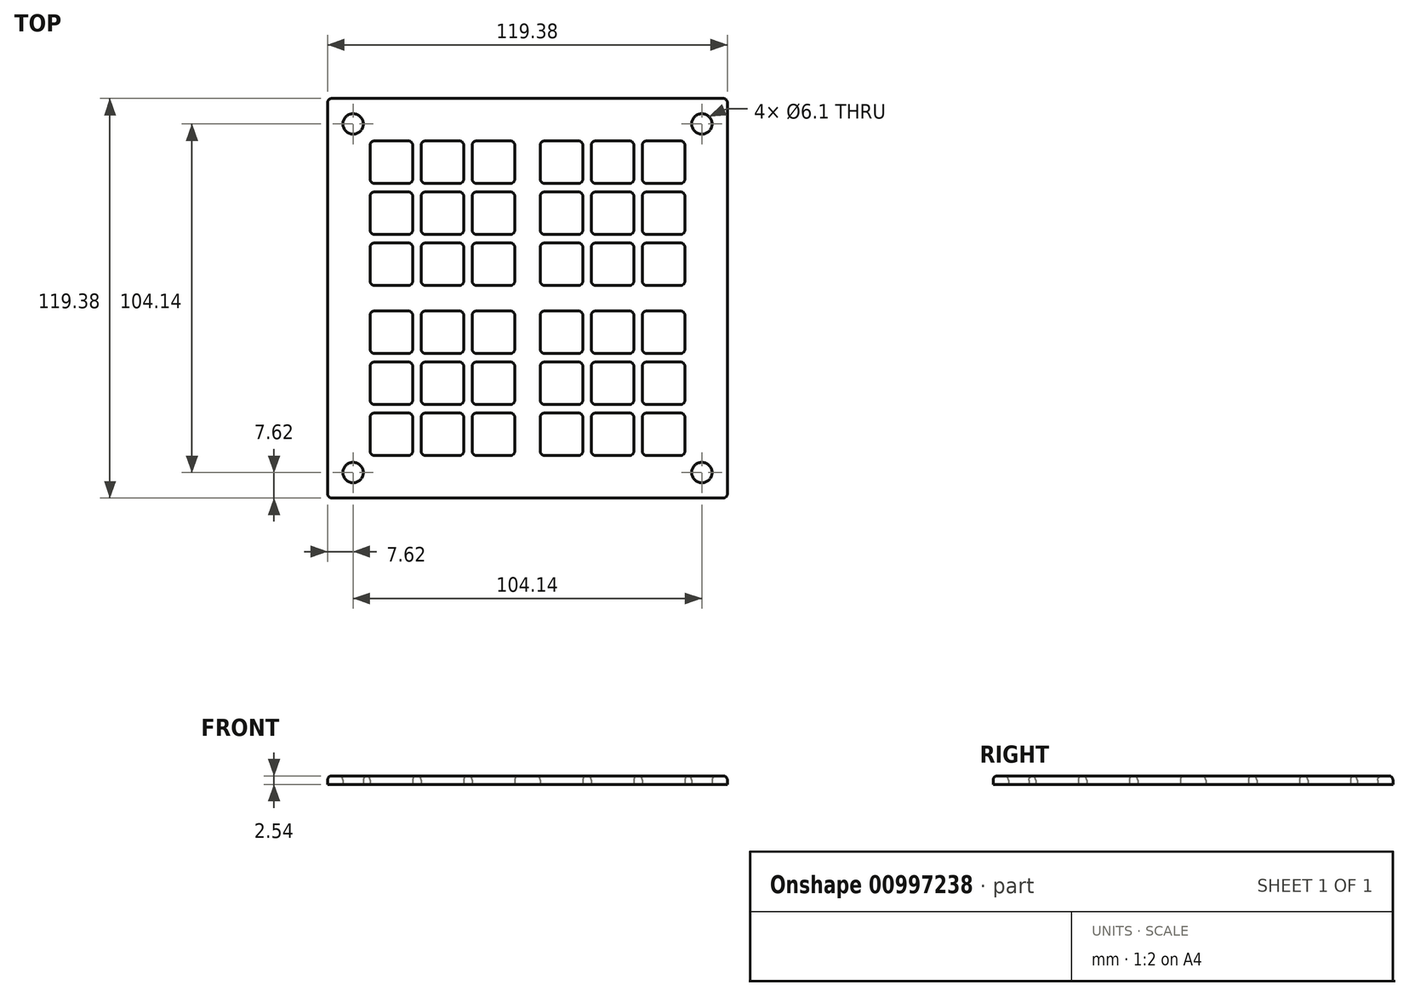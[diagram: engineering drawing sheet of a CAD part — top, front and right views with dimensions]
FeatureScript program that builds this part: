
annotation { "Feature Type Name" : "Feature", "Feature Type Description" : "" }
export const myFeature = defineFeature(function(context is Context, id is Id, definition is map)
    precondition{}
    {
        {
            var Q0;
            Q0=qCreatedBy(makeId("Top.planeOp"),FACE);
            var sketch = newSketch(context, id + "F0", { "sketchPlane" : qUnion([Q0])});
            skLineSegment(sketch, "E0.bottom", {"start": v(59.69, -59.7) * mm, "end": v(-59.7, -59.69) * mm});
            skLineSegment(sketch, "E0.top", {"start": v(59.7, 59.69) * mm, "end": v(-59.7, 59.7) * mm});
            skLineSegment(sketch, "E0.left", {"start": v(59.69, -59.7) * mm, "end": v(59.7, 59.69) * mm});
            skLineSegment(sketch, "E0.right", {"start": v(-59.7, -59.69) * mm, "end": v(-59.69, 59.69) * mm});
            skPoint(sketch, "E0.middle", {"position": v(0, 0) * mm});
            skCircle(sketch, "E1", {"center": v(52.07, -52.07) * mm, "radius": 3.05 * mm});
            skLineSegment(sketch, "E2", {"start": v(0, 59.7) * mm, "end": v(0, -59.7) * mm, "construction": true});
            skLineSegment(sketch, "E3", {"start": v(59.7, 0) * mm, "end": v(-59.7, 0) * mm, "construction": true});
            skCircle(sketch, "E4.MirrorC", {"center": v(-52.07, -52.07) * mm, "radius": 3.05 * mm});
            skCircle(sketch, "E5.MirrorC", {"center": v(52.07, 52.07) * mm, "radius": 3.05 * mm});
            skCircle(sketch, "E6.MirrorC", {"center": v(-52.07, 52.07) * mm, "radius": 3.05 * mm});
            skLineSegment(sketch, "E7.bottom", {"start": v(35.56, -34.3) * mm, "end": v(45.72, -34.3) * mm});
            skLineSegment(sketch, "E7.top", {"start": v(35.56, -47) * mm, "end": v(45.72, -47) * mm});
            skLineSegment(sketch, "E7.left", {"start": v(34.3, -35.56) * mm, "end": v(34.3, -45.72) * mm});
            skLineSegment(sketch, "E7.right", {"start": v(47, -35.56) * mm, "end": v(47, -45.72) * mm});
            skPoint(sketch, "E7.middle", {"position": v(40.64, -40.64) * mm});
            skPoint(sketch, "E8.visualSharp", {"position": v(46.99, -47) * mm});
            skArc(sketch, "E8.filletArc", {"start": v(45.72, -47) * mm, "mid": v(46.62, -46.62) * mm, "end": v(46.99, -45.72) * mm});
            skPoint(sketch, "E9.visualSharp", {"position": v(34.3, -47) * mm});
            skArc(sketch, "E9.filletArc", {"start": v(34.3, -45.72) * mm, "mid": v(34.66, -46.62) * mm, "end": v(35.56, -47) * mm});
            skPoint(sketch, "E10.visualSharp", {"position": v(34.3, -34.3) * mm});
            skArc(sketch, "E10.filletArc", {"start": v(35.56, -34.3) * mm, "mid": v(34.66, -34.66) * mm, "end": v(34.3, -35.56) * mm});
            skPoint(sketch, "E11.visualSharp", {"position": v(47, -34.3) * mm});
            skArc(sketch, "E11.filletArc", {"start": v(47, -35.56) * mm, "mid": v(46.62, -34.66) * mm, "end": v(45.72, -34.3) * mm});
            skLineSegment(sketch, "E12.0.1.0", {"start": v(34.3, -20.32) * mm, "end": v(34.3, -30.48) * mm});
            skLineSegment(sketch, "E12.0.1.1", {"start": v(35.56, -31.75) * mm, "end": v(45.72, -31.75) * mm});
            skLineSegment(sketch, "E12.0.1.2", {"start": v(47, -20.32) * mm, "end": v(47, -30.48) * mm});
            skLineSegment(sketch, "E12.0.1.3", {"start": v(35.56, -19.05) * mm, "end": v(45.72, -19.05) * mm});
            skArc(sketch, "E12.0.1.4", {"start": v(35.56, -19.05) * mm, "mid": v(34.66, -19.42) * mm, "end": v(34.3, -20.32) * mm});
            skArc(sketch, "E12.0.1.5", {"start": v(47, -20.32) * mm, "mid": v(46.62, -19.42) * mm, "end": v(45.72, -19.05) * mm});
            skArc(sketch, "E12.0.1.6", {"start": v(45.72, -31.75) * mm, "mid": v(46.62, -31.38) * mm, "end": v(46.99, -30.48) * mm});
            skArc(sketch, "E12.0.1.7", {"start": v(34.3, -30.48) * mm, "mid": v(34.66, -31.38) * mm, "end": v(35.56, -31.75) * mm});
            skLineSegment(sketch, "E12.0.2.0", {"start": v(34.3, -5.08) * mm, "end": v(34.3, -15.24) * mm});
            skLineSegment(sketch, "E12.0.2.1", {"start": v(35.56, -16.51) * mm, "end": v(45.72, -16.51) * mm});
            skLineSegment(sketch, "E12.0.2.2", {"start": v(47, -5.08) * mm, "end": v(47, -15.24) * mm});
            skLineSegment(sketch, "E12.0.2.3", {"start": v(35.56, -3.81) * mm, "end": v(45.72, -3.81) * mm});
            skArc(sketch, "E12.0.2.4", {"start": v(35.56, -3.81) * mm, "mid": v(34.66, -4.18) * mm, "end": v(34.3, -5.08) * mm});
            skArc(sketch, "E12.0.2.5", {"start": v(47, -5.08) * mm, "mid": v(46.62, -4.18) * mm, "end": v(45.72, -3.81) * mm});
            skArc(sketch, "E12.0.2.6", {"start": v(45.72, -16.51) * mm, "mid": v(46.62, -16.14) * mm, "end": v(46.99, -15.24) * mm});
            skArc(sketch, "E12.0.2.7", {"start": v(34.3, -15.24) * mm, "mid": v(34.66, -16.14) * mm, "end": v(35.56, -16.51) * mm});
            skLineSegment(sketch, "E12.1.0.0", {"start": v(19.05, -35.56) * mm, "end": v(19.05, -45.72) * mm});
            skLineSegment(sketch, "E12.1.0.1", {"start": v(20.32, -47) * mm, "end": v(30.48, -47) * mm});
            skLineSegment(sketch, "E12.1.0.2", {"start": v(31.75, -35.56) * mm, "end": v(31.75, -45.72) * mm});
            skLineSegment(sketch, "E12.1.0.3", {"start": v(20.32, -34.3) * mm, "end": v(30.48, -34.3) * mm});
            skArc(sketch, "E12.1.0.4", {"start": v(20.32, -34.3) * mm, "mid": v(19.42, -34.66) * mm, "end": v(19.05, -35.56) * mm});
            skArc(sketch, "E12.1.0.5", {"start": v(31.75, -35.56) * mm, "mid": v(31.38, -34.66) * mm, "end": v(30.48, -34.3) * mm});
            skArc(sketch, "E12.1.0.6", {"start": v(30.48, -47) * mm, "mid": v(31.38, -46.62) * mm, "end": v(31.75, -45.72) * mm});
            skArc(sketch, "E12.1.0.7", {"start": v(19.05, -45.72) * mm, "mid": v(19.42, -46.62) * mm, "end": v(20.32, -47) * mm});
            skLineSegment(sketch, "E12.1.1.0", {"start": v(19.05, -20.32) * mm, "end": v(19.05, -30.48) * mm});
            skLineSegment(sketch, "E12.1.1.1", {"start": v(20.32, -31.75) * mm, "end": v(30.48, -31.75) * mm});
            skLineSegment(sketch, "E12.1.1.2", {"start": v(31.75, -20.32) * mm, "end": v(31.75, -30.48) * mm});
            skLineSegment(sketch, "E12.1.1.3", {"start": v(20.32, -19.05) * mm, "end": v(30.48, -19.05) * mm});
            skArc(sketch, "E12.1.1.4", {"start": v(20.32, -19.05) * mm, "mid": v(19.42, -19.42) * mm, "end": v(19.05, -20.32) * mm});
            skArc(sketch, "E12.1.1.5", {"start": v(31.75, -20.32) * mm, "mid": v(31.38, -19.42) * mm, "end": v(30.48, -19.05) * mm});
            skArc(sketch, "E12.1.1.6", {"start": v(30.48, -31.75) * mm, "mid": v(31.38, -31.38) * mm, "end": v(31.75, -30.48) * mm});
            skArc(sketch, "E12.1.1.7", {"start": v(19.05, -30.48) * mm, "mid": v(19.42, -31.38) * mm, "end": v(20.32, -31.75) * mm});
            skLineSegment(sketch, "E12.1.2.0", {"start": v(19.05, -5.08) * mm, "end": v(19.05, -15.24) * mm});
            skLineSegment(sketch, "E12.1.2.1", {"start": v(20.32, -16.51) * mm, "end": v(30.48, -16.51) * mm});
            skLineSegment(sketch, "E12.1.2.2", {"start": v(31.75, -5.08) * mm, "end": v(31.75, -15.24) * mm});
            skLineSegment(sketch, "E12.1.2.3", {"start": v(20.32, -3.81) * mm, "end": v(30.48, -3.81) * mm});
            skArc(sketch, "E12.1.2.4", {"start": v(20.32, -3.81) * mm, "mid": v(19.42, -4.18) * mm, "end": v(19.05, -5.08) * mm});
            skArc(sketch, "E12.1.2.5", {"start": v(31.75, -5.08) * mm, "mid": v(31.38, -4.18) * mm, "end": v(30.48, -3.81) * mm});
            skArc(sketch, "E12.1.2.6", {"start": v(30.48, -16.51) * mm, "mid": v(31.38, -16.14) * mm, "end": v(31.75, -15.24) * mm});
            skArc(sketch, "E12.1.2.7", {"start": v(19.05, -15.24) * mm, "mid": v(19.42, -16.14) * mm, "end": v(20.32, -16.51) * mm});
            skLineSegment(sketch, "E12.2.0.0", {"start": v(3.81, -35.56) * mm, "end": v(3.81, -45.72) * mm});
            skLineSegment(sketch, "E12.2.0.1", {"start": v(5.08, -47) * mm, "end": v(15.24, -47) * mm});
            skLineSegment(sketch, "E12.2.0.2", {"start": v(16.51, -35.56) * mm, "end": v(16.51, -45.72) * mm});
            skLineSegment(sketch, "E12.2.0.3", {"start": v(5.08, -34.3) * mm, "end": v(15.24, -34.3) * mm});
            skArc(sketch, "E12.2.0.4", {"start": v(5.08, -34.3) * mm, "mid": v(4.18, -34.66) * mm, "end": v(3.81, -35.56) * mm});
            skArc(sketch, "E12.2.0.5", {"start": v(16.51, -35.56) * mm, "mid": v(16.14, -34.66) * mm, "end": v(15.24, -34.3) * mm});
            skArc(sketch, "E12.2.0.6", {"start": v(15.24, -47) * mm, "mid": v(16.14, -46.62) * mm, "end": v(16.51, -45.72) * mm});
            skArc(sketch, "E12.2.0.7", {"start": v(3.81, -45.72) * mm, "mid": v(4.18, -46.62) * mm, "end": v(5.08, -47) * mm});
            skLineSegment(sketch, "E12.2.1.0", {"start": v(3.81, -20.32) * mm, "end": v(3.81, -30.48) * mm});
            skLineSegment(sketch, "E12.2.1.1", {"start": v(5.08, -31.75) * mm, "end": v(15.24, -31.75) * mm});
            skLineSegment(sketch, "E12.2.1.2", {"start": v(16.51, -20.32) * mm, "end": v(16.51, -30.48) * mm});
            skLineSegment(sketch, "E12.2.1.3", {"start": v(5.08, -19.05) * mm, "end": v(15.24, -19.05) * mm});
            skArc(sketch, "E12.2.1.4", {"start": v(5.08, -19.05) * mm, "mid": v(4.18, -19.42) * mm, "end": v(3.81, -20.32) * mm});
            skArc(sketch, "E12.2.1.5", {"start": v(16.51, -20.32) * mm, "mid": v(16.14, -19.42) * mm, "end": v(15.24, -19.05) * mm});
            skArc(sketch, "E12.2.1.6", {"start": v(15.24, -31.75) * mm, "mid": v(16.14, -31.38) * mm, "end": v(16.51, -30.48) * mm});
            skArc(sketch, "E12.2.1.7", {"start": v(3.81, -30.48) * mm, "mid": v(4.18, -31.38) * mm, "end": v(5.08, -31.75) * mm});
            skLineSegment(sketch, "E12.2.2.0", {"start": v(3.81, -5.08) * mm, "end": v(3.81, -15.24) * mm});
            skLineSegment(sketch, "E12.2.2.1", {"start": v(5.08, -16.51) * mm, "end": v(15.24, -16.51) * mm});
            skLineSegment(sketch, "E12.2.2.2", {"start": v(16.51, -5.08) * mm, "end": v(16.51, -15.24) * mm});
            skLineSegment(sketch, "E12.2.2.3", {"start": v(5.08, -3.81) * mm, "end": v(15.24, -3.81) * mm});
            skArc(sketch, "E12.2.2.4", {"start": v(5.08, -3.81) * mm, "mid": v(4.18, -4.18) * mm, "end": v(3.81, -5.08) * mm});
            skArc(sketch, "E12.2.2.5", {"start": v(16.51, -5.08) * mm, "mid": v(16.14, -4.18) * mm, "end": v(15.24, -3.81) * mm});
            skArc(sketch, "E12.2.2.6", {"start": v(15.24, -16.51) * mm, "mid": v(16.14, -16.14) * mm, "end": v(16.51, -15.24) * mm});
            skArc(sketch, "E12.2.2.7", {"start": v(3.81, -15.24) * mm, "mid": v(4.18, -16.14) * mm, "end": v(5.08, -16.51) * mm});
            skLineSegment(sketch, "E12.direction1", {"start": v(36.51, -44.77) * mm, "end": v(21.27, -44.77) * mm, "construction": true});
            skLineSegment(sketch, "E12.direction2", {"start": v(36.51, -44.77) * mm, "end": v(36.51, -29.53) * mm, "construction": true});
            skArc(sketch, "E13.MirrorCS", {"start": v(-47, -35.56) * mm, "mid": v(-46.62, -34.66) * mm, "end": v(-45.72, -34.3) * mm});
            skArc(sketch, "E14.MirrorCS", {"start": v(-35.56, -34.3) * mm, "mid": v(-34.66, -34.66) * mm, "end": v(-34.29, -35.56) * mm});
            skArc(sketch, "E15.MirrorCS", {"start": v(-34.3, -45.72) * mm, "mid": v(-34.66, -46.62) * mm, "end": v(-35.56, -47) * mm});
            skArc(sketch, "E16.MirrorCS", {"start": v(-45.72, -47) * mm, "mid": v(-46.62, -46.62) * mm, "end": v(-46.99, -45.72) * mm});
            skArc(sketch, "E17.MirrorCS", {"start": v(-34.29, -30.48) * mm, "mid": v(-34.66, -31.38) * mm, "end": v(-35.56, -31.75) * mm});
            skArc(sketch, "E18.MirrorCS", {"start": v(-20.32, -19.05) * mm, "mid": v(-19.42, -19.42) * mm, "end": v(-19.05, -20.32) * mm});
            skArc(sketch, "E19.MirrorCS", {"start": v(-5.08, -34.3) * mm, "mid": v(-4.18, -34.66) * mm, "end": v(-3.8, -35.56) * mm});
            skArc(sketch, "E20.MirrorCS", {"start": v(-5.08, -3.81) * mm, "mid": v(-4.18, -4.18) * mm, "end": v(-3.81, -5.08) * mm});
            skArc(sketch, "E21.MirrorCS", {"start": v(-35.56, -3.81) * mm, "mid": v(-34.66, -4.18) * mm, "end": v(-34.3, -5.08) * mm});
            skArc(sketch, "E22.MirrorCS", {"start": v(-15.24, -47) * mm, "mid": v(-16.14, -46.62) * mm, "end": v(-16.5, -45.72) * mm});
            skArc(sketch, "E23.MirrorCS", {"start": v(-45.72, -16.51) * mm, "mid": v(-46.62, -16.14) * mm, "end": v(-46.99, -15.24) * mm});
            skArc(sketch, "E24.MirrorCS", {"start": v(-30.48, -47) * mm, "mid": v(-31.38, -46.62) * mm, "end": v(-31.75, -45.72) * mm});
            skArc(sketch, "E25.MirrorCS", {"start": v(-16.51, -5.08) * mm, "mid": v(-16.14, -4.18) * mm, "end": v(-15.24, -3.81) * mm});
            skArc(sketch, "E26.MirrorCS", {"start": v(-19.05, -30.48) * mm, "mid": v(-19.42, -31.38) * mm, "end": v(-20.32, -31.75) * mm});
            skArc(sketch, "E27.MirrorCS", {"start": v(-3.81, -15.24) * mm, "mid": v(-4.18, -16.14) * mm, "end": v(-5.08, -16.51) * mm});
            skArc(sketch, "E28.MirrorCS", {"start": v(-16.51, -35.56) * mm, "mid": v(-16.14, -34.66) * mm, "end": v(-15.24, -34.3) * mm});
            skArc(sketch, "E29.MirrorCS", {"start": v(-31.75, -20.32) * mm, "mid": v(-31.38, -19.42) * mm, "end": v(-30.48, -19.05) * mm});
            skArc(sketch, "E30.MirrorCS", {"start": v(-15.24, -31.75) * mm, "mid": v(-16.14, -31.38) * mm, "end": v(-16.5, -30.48) * mm});
            skArc(sketch, "E31.MirrorCS", {"start": v(-16.51, -20.32) * mm, "mid": v(-16.14, -19.42) * mm, "end": v(-15.24, -19.05) * mm});
            skArc(sketch, "E32.MirrorCS", {"start": v(-47, -20.32) * mm, "mid": v(-46.62, -19.42) * mm, "end": v(-45.72, -19.05) * mm});
            skArc(sketch, "E33.MirrorCS", {"start": v(-31.75, -35.56) * mm, "mid": v(-31.38, -34.66) * mm, "end": v(-30.48, -34.3) * mm});
            skArc(sketch, "E34.MirrorCS", {"start": v(-31.75, -5.08) * mm, "mid": v(-31.38, -4.18) * mm, "end": v(-30.48, -3.81) * mm});
            skArc(sketch, "E35.MirrorCS", {"start": v(-3.81, -30.48) * mm, "mid": v(-4.18, -31.38) * mm, "end": v(-5.08, -31.75) * mm});
            skArc(sketch, "E36.MirrorCS", {"start": v(-19.05, -45.72) * mm, "mid": v(-19.42, -46.62) * mm, "end": v(-20.32, -47) * mm});
            skArc(sketch, "E37.MirrorCS", {"start": v(-19.05, -15.24) * mm, "mid": v(-19.42, -16.14) * mm, "end": v(-20.32, -16.51) * mm});
            skArc(sketch, "E38.MirrorCS", {"start": v(-30.48, -31.75) * mm, "mid": v(-31.38, -31.38) * mm, "end": v(-31.75, -30.48) * mm});
            skArc(sketch, "E39.MirrorCS", {"start": v(-15.24, -16.51) * mm, "mid": v(-16.14, -16.14) * mm, "end": v(-16.51, -15.24) * mm});
            skArc(sketch, "E40.MirrorCS", {"start": v(-5.08, -19.05) * mm, "mid": v(-4.18, -19.42) * mm, "end": v(-3.81, -20.32) * mm});
            skArc(sketch, "E41.MirrorCS", {"start": v(-35.56, -19.05) * mm, "mid": v(-34.66, -19.42) * mm, "end": v(-34.3, -20.32) * mm});
            skArc(sketch, "E42.MirrorCS", {"start": v(-20.32, -34.3) * mm, "mid": v(-19.42, -34.66) * mm, "end": v(-19.05, -35.56) * mm});
            skArc(sketch, "E43.MirrorCS", {"start": v(-20.32, -3.81) * mm, "mid": v(-19.42, -4.18) * mm, "end": v(-19.05, -5.08) * mm});
            skArc(sketch, "E44.MirrorCS", {"start": v(-30.48, -16.51) * mm, "mid": v(-31.38, -16.14) * mm, "end": v(-31.75, -15.24) * mm});
            skArc(sketch, "E45.MirrorCS", {"start": v(-45.72, -31.75) * mm, "mid": v(-46.62, -31.38) * mm, "end": v(-46.99, -30.48) * mm});
            skArc(sketch, "E46.MirrorCS", {"start": v(-34.3, -15.24) * mm, "mid": v(-34.66, -16.14) * mm, "end": v(-35.56, -16.51) * mm});
            skArc(sketch, "E47.MirrorCS", {"start": v(-3.8, -45.72) * mm, "mid": v(-4.18, -46.62) * mm, "end": v(-5.08, -47) * mm});
            skArc(sketch, "E48.MirrorCS", {"start": v(-47, -5.08) * mm, "mid": v(-46.62, -4.18) * mm, "end": v(-45.72, -3.81) * mm});
            skLineSegment(sketch, "E49.MirrorCS", {"start": v(-5.08, -19.05) * mm, "end": v(-15.24, -19.05) * mm});
            skLineSegment(sketch, "E50.MirrorCS", {"start": v(-35.56, -19.05) * mm, "end": v(-45.72, -19.05) * mm});
            skLineSegment(sketch, "E51.MirrorCS", {"start": v(-20.32, -34.3) * mm, "end": v(-30.48, -34.3) * mm});
            skLineSegment(sketch, "E52.MirrorCS", {"start": v(-20.32, -3.81) * mm, "end": v(-30.48, -3.81) * mm});
            skLineSegment(sketch, "E53.MirrorCS", {"start": v(-46.99, -35.56) * mm, "end": v(-46.99, -45.72) * mm});
            skLineSegment(sketch, "E54.MirrorCS", {"start": v(-5.08, -31.75) * mm, "end": v(-15.24, -31.75) * mm});
            skLineSegment(sketch, "E55.MirrorCS", {"start": v(-36.51, -44.77) * mm, "end": v(-36.51, -29.53) * mm, "construction": true});
            skLineSegment(sketch, "E56.MirrorCS", {"start": v(-34.29, -35.56) * mm, "end": v(-34.29, -45.72) * mm});
            skLineSegment(sketch, "E57.MirrorCS", {"start": v(-20.32, -47) * mm, "end": v(-30.48, -47) * mm});
            skLineSegment(sketch, "E58.MirrorCS", {"start": v(-20.32, -16.51) * mm, "end": v(-30.48, -16.51) * mm});
            skLineSegment(sketch, "E59.MirrorCS", {"start": v(-3.81, -20.32) * mm, "end": v(-3.8, -30.48) * mm});
            skLineSegment(sketch, "E60.MirrorCS", {"start": v(-35.56, -47) * mm, "end": v(-45.72, -47) * mm});
            skLineSegment(sketch, "E61.MirrorCS", {"start": v(-36.51, -44.77) * mm, "end": v(-21.27, -44.77) * mm, "construction": true});
            skPoint(sketch, "E62.MirrorP", {"position": v(-34.29, -34.3) * mm});
            skLineSegment(sketch, "E63.MirrorCS", {"start": v(-35.56, -34.3) * mm, "end": v(-45.72, -34.3) * mm});
            skLineSegment(sketch, "E64.MirrorCS", {"start": v(-19.05, -35.56) * mm, "end": v(-19.05, -45.72) * mm});
            skLineSegment(sketch, "E65.MirrorCS", {"start": v(-19.05, -5.08) * mm, "end": v(-19.05, -15.24) * mm});
            skLineSegment(sketch, "E66.MirrorCS", {"start": v(-19.05, -20.32) * mm, "end": v(-19.05, -30.48) * mm});
            skLineSegment(sketch, "E67.MirrorCS", {"start": v(-3.81, -35.56) * mm, "end": v(-3.8, -45.72) * mm});
            skLineSegment(sketch, "E68.MirrorCS", {"start": v(-3.81, -5.08) * mm, "end": v(-3.81, -15.24) * mm});
            skLineSegment(sketch, "E69.MirrorCS", {"start": v(-34.3, -5.08) * mm, "end": v(-34.3, -15.24) * mm});
            skLineSegment(sketch, "E70.MirrorCS", {"start": v(-31.75, -20.32) * mm, "end": v(-31.75, -30.48) * mm});
            skLineSegment(sketch, "E71.MirrorCS", {"start": v(-16.51, -35.56) * mm, "end": v(-16.51, -45.72) * mm});
            skLineSegment(sketch, "E72.MirrorCS", {"start": v(-16.51, -5.08) * mm, "end": v(-16.51, -15.24) * mm});
            skLineSegment(sketch, "E73.MirrorCS", {"start": v(-47, -5.08) * mm, "end": v(-47, -15.24) * mm});
            skPoint(sketch, "E74.MirrorP", {"position": v(-46.99, -47) * mm});
            skPoint(sketch, "E75.MirrorP", {"position": v(-34.29, -47) * mm});
            skLineSegment(sketch, "E76.MirrorCS", {"start": v(-34.3, -20.32) * mm, "end": v(-34.3, -30.48) * mm});
            skLineSegment(sketch, "E77.MirrorCS", {"start": v(-35.56, -31.75) * mm, "end": v(-45.72, -31.75) * mm});
            skLineSegment(sketch, "E78.MirrorCS", {"start": v(-16.51, -20.32) * mm, "end": v(-16.51, -30.48) * mm});
            skPoint(sketch, "E79.MirrorP", {"position": v(-46.99, -34.3) * mm});
            skLineSegment(sketch, "E80.MirrorCS", {"start": v(-47, -20.32) * mm, "end": v(-47, -30.48) * mm});
            skLineSegment(sketch, "E81.MirrorCS", {"start": v(-31.75, -35.56) * mm, "end": v(-31.75, -45.72) * mm});
            skLineSegment(sketch, "E82.MirrorCS", {"start": v(-31.75, -5.08) * mm, "end": v(-31.75, -15.24) * mm});
            skPoint(sketch, "E83.MirrorP", {"position": v(-40.64, -40.64) * mm});
            skLineSegment(sketch, "E84.MirrorCS", {"start": v(-20.32, -31.75) * mm, "end": v(-30.48, -31.75) * mm});
            skLineSegment(sketch, "E85.MirrorCS", {"start": v(-35.56, -16.51) * mm, "end": v(-45.72, -16.51) * mm});
            skLineSegment(sketch, "E86.MirrorCS", {"start": v(-5.08, -3.81) * mm, "end": v(-15.24, -3.81) * mm});
            skLineSegment(sketch, "E87.MirrorCS", {"start": v(-20.32, -19.05) * mm, "end": v(-30.48, -19.05) * mm});
            skLineSegment(sketch, "E88.MirrorCS", {"start": v(-35.56, -3.81) * mm, "end": v(-45.72, -3.81) * mm});
            skLineSegment(sketch, "E89.MirrorCS", {"start": v(-5.08, -34.3) * mm, "end": v(-15.24, -34.3) * mm});
            skLineSegment(sketch, "E90.MirrorCS", {"start": v(-5.08, -16.51) * mm, "end": v(-15.24, -16.51) * mm});
            skLineSegment(sketch, "E91.MirrorCS", {"start": v(-5.08, -47) * mm, "end": v(-15.24, -47) * mm});
            skArc(sketch, "E92.MirrorCS", {"start": v(-34.3, 45.72) * mm, "mid": v(-34.66, 46.62) * mm, "end": v(-35.56, 47) * mm});
            skArc(sketch, "E93.MirrorCS", {"start": v(-35.56, 34.3) * mm, "mid": v(-34.66, 34.66) * mm, "end": v(-34.29, 35.56) * mm});
            skArc(sketch, "E94.MirrorCS", {"start": v(-35.56, 19.05) * mm, "mid": v(-34.66, 19.42) * mm, "end": v(-34.3, 20.32) * mm});
            skArc(sketch, "E95.MirrorCS", {"start": v(-16.51, 5.08) * mm, "mid": v(-16.14, 4.18) * mm, "end": v(-15.24, 3.81) * mm});
            skArc(sketch, "E96.MirrorCS", {"start": v(45.72, 31.75) * mm, "mid": v(46.62, 31.38) * mm, "end": v(46.99, 30.48) * mm});
            skArc(sketch, "E97.MirrorCS", {"start": v(35.56, 19.05) * mm, "mid": v(34.66, 19.42) * mm, "end": v(34.3, 20.32) * mm});
            skArc(sketch, "E98.MirrorCS", {"start": v(45.72, 47) * mm, "mid": v(46.62, 46.62) * mm, "end": v(46.99, 45.72) * mm});
            skArc(sketch, "E99.MirrorCS", {"start": v(-15.24, 16.51) * mm, "mid": v(-16.14, 16.14) * mm, "end": v(-16.51, 15.24) * mm});
            skArc(sketch, "E100.MirrorCS", {"start": v(20.32, 19.05) * mm, "mid": v(19.42, 19.42) * mm, "end": v(19.05, 20.32) * mm});
            skArc(sketch, "E101.MirrorCS", {"start": v(-15.24, 47) * mm, "mid": v(-16.14, 46.62) * mm, "end": v(-16.51, 45.72) * mm});
            skArc(sketch, "E102.MirrorCS", {"start": v(-30.48, 31.75) * mm, "mid": v(-31.38, 31.38) * mm, "end": v(-31.75, 30.48) * mm});
            skArc(sketch, "E103.MirrorCS", {"start": v(47, 35.56) * mm, "mid": v(46.62, 34.66) * mm, "end": v(45.72, 34.3) * mm});
            skArc(sketch, "E104.MirrorCS", {"start": v(5.08, 3.81) * mm, "mid": v(4.18, 4.18) * mm, "end": v(3.81, 5.08) * mm});
            skArc(sketch, "E105.MirrorCS", {"start": v(-30.48, 47) * mm, "mid": v(-31.38, 46.62) * mm, "end": v(-31.75, 45.72) * mm});
            skArc(sketch, "E106.MirrorCS", {"start": v(-45.72, 16.51) * mm, "mid": v(-46.62, 16.14) * mm, "end": v(-47, 15.24) * mm});
            skArc(sketch, "E107.MirrorCS", {"start": v(5.08, 34.3) * mm, "mid": v(4.18, 34.66) * mm, "end": v(3.8, 35.56) * mm});
            skArc(sketch, "E108.MirrorCS", {"start": v(35.56, 3.81) * mm, "mid": v(34.66, 4.18) * mm, "end": v(34.3, 5.08) * mm});
            skArc(sketch, "E109.MirrorCS", {"start": v(-16.51, 20.32) * mm, "mid": v(-16.14, 19.42) * mm, "end": v(-15.24, 19.05) * mm});
            skArc(sketch, "E110.MirrorCS", {"start": v(16.51, 35.56) * mm, "mid": v(16.14, 34.66) * mm, "end": v(15.24, 34.3) * mm});
            skArc(sketch, "E111.MirrorCS", {"start": v(-16.51, 35.56) * mm, "mid": v(-16.14, 34.66) * mm, "end": v(-15.24, 34.3) * mm});
            skArc(sketch, "E112.MirrorCS", {"start": v(35.56, 34.3) * mm, "mid": v(34.66, 34.66) * mm, "end": v(34.29, 35.56) * mm});
            skArc(sketch, "E113.MirrorCS", {"start": v(34.3, 45.72) * mm, "mid": v(34.66, 46.62) * mm, "end": v(35.56, 47) * mm});
            skArc(sketch, "E114.MirrorCS", {"start": v(-45.72, 47) * mm, "mid": v(-46.62, 46.62) * mm, "end": v(-46.99, 45.72) * mm});
            skArc(sketch, "E115.MirrorCS", {"start": v(-5.08, 19.05) * mm, "mid": v(-4.18, 19.42) * mm, "end": v(-3.81, 20.32) * mm});
            skArc(sketch, "E116.MirrorCS", {"start": v(-15.24, 31.75) * mm, "mid": v(-16.14, 31.38) * mm, "end": v(-16.51, 30.48) * mm});
            skArc(sketch, "E117.MirrorCS", {"start": v(-34.3, 15.24) * mm, "mid": v(-34.66, 16.14) * mm, "end": v(-35.56, 16.51) * mm});
            skArc(sketch, "E118.MirrorCS", {"start": v(3.81, 30.48) * mm, "mid": v(4.18, 31.38) * mm, "end": v(5.08, 31.75) * mm});
            skArc(sketch, "E119.MirrorCS", {"start": v(-20.32, 19.05) * mm, "mid": v(-19.42, 19.42) * mm, "end": v(-19.05, 20.32) * mm});
            skArc(sketch, "E120.MirrorCS", {"start": v(-3.81, 15.24) * mm, "mid": v(-4.18, 16.14) * mm, "end": v(-5.08, 16.51) * mm});
            skArc(sketch, "E121.MirrorCS", {"start": v(-31.75, 5.08) * mm, "mid": v(-31.38, 4.18) * mm, "end": v(-30.48, 3.81) * mm});
            skArc(sketch, "E122.MirrorCS", {"start": v(-20.32, 3.81) * mm, "mid": v(-19.42, 4.18) * mm, "end": v(-19.05, 5.08) * mm});
            skArc(sketch, "E123.MirrorCS", {"start": v(34.29, 30.48) * mm, "mid": v(34.66, 31.38) * mm, "end": v(35.56, 31.75) * mm});
            skArc(sketch, "E124.MirrorCS", {"start": v(19.05, 45.72) * mm, "mid": v(19.42, 46.62) * mm, "end": v(20.32, 47) * mm});
            skArc(sketch, "E125.MirrorCS", {"start": v(19.05, 15.24) * mm, "mid": v(19.42, 16.14) * mm, "end": v(20.32, 16.51) * mm});
            skArc(sketch, "E126.MirrorCS", {"start": v(-19.05, 15.24) * mm, "mid": v(-19.42, 16.14) * mm, "end": v(-20.32, 16.51) * mm});
            skArc(sketch, "E127.MirrorCS", {"start": v(-35.56, 3.81) * mm, "mid": v(-34.66, 4.18) * mm, "end": v(-34.3, 5.08) * mm});
            skArc(sketch, "E128.MirrorCS", {"start": v(30.48, 31.75) * mm, "mid": v(31.38, 31.38) * mm, "end": v(31.75, 30.48) * mm});
            skArc(sketch, "E129.MirrorCS", {"start": v(15.24, 47) * mm, "mid": v(16.14, 46.62) * mm, "end": v(16.5, 45.72) * mm});
            skArc(sketch, "E130.MirrorCS", {"start": v(15.24, 16.51) * mm, "mid": v(16.14, 16.14) * mm, "end": v(16.51, 15.24) * mm});
            skArc(sketch, "E131.MirrorCS", {"start": v(45.72, 16.51) * mm, "mid": v(46.62, 16.14) * mm, "end": v(47, 15.24) * mm});
            skArc(sketch, "E132.MirrorCS", {"start": v(-47, 35.56) * mm, "mid": v(-46.62, 34.66) * mm, "end": v(-45.72, 34.3) * mm});
            skArc(sketch, "E133.MirrorCS", {"start": v(-31.75, 20.32) * mm, "mid": v(-31.38, 19.42) * mm, "end": v(-30.48, 19.05) * mm});
            skArc(sketch, "E134.MirrorCS", {"start": v(-45.72, 31.75) * mm, "mid": v(-46.62, 31.38) * mm, "end": v(-46.99, 30.48) * mm});
            skArc(sketch, "E135.MirrorCS", {"start": v(15.24, 31.75) * mm, "mid": v(16.14, 31.38) * mm, "end": v(16.5, 30.48) * mm});
            skArc(sketch, "E136.MirrorCS", {"start": v(3.8, 45.72) * mm, "mid": v(4.18, 46.62) * mm, "end": v(5.08, 47) * mm});
            skArc(sketch, "E137.MirrorCS", {"start": v(3.81, 15.24) * mm, "mid": v(4.18, 16.14) * mm, "end": v(5.08, 16.51) * mm});
            skArc(sketch, "E138.MirrorCS", {"start": v(-34.29, 30.48) * mm, "mid": v(-34.66, 31.38) * mm, "end": v(-35.56, 31.75) * mm});
            skArc(sketch, "E139.MirrorCS", {"start": v(-19.05, 30.48) * mm, "mid": v(-19.42, 31.38) * mm, "end": v(-20.32, 31.75) * mm});
            skArc(sketch, "E140.MirrorCS", {"start": v(-31.75, 35.56) * mm, "mid": v(-31.38, 34.66) * mm, "end": v(-30.48, 34.3) * mm});
            skArc(sketch, "E141.MirrorCS", {"start": v(-20.32, 34.3) * mm, "mid": v(-19.42, 34.66) * mm, "end": v(-19.05, 35.56) * mm});
            skArc(sketch, "E142.MirrorCS", {"start": v(30.48, 47) * mm, "mid": v(31.38, 46.62) * mm, "end": v(31.75, 45.72) * mm});
            skArc(sketch, "E143.MirrorCS", {"start": v(34.3, 15.24) * mm, "mid": v(34.66, 16.14) * mm, "end": v(35.56, 16.51) * mm});
            skArc(sketch, "E144.MirrorCS", {"start": v(30.48, 16.51) * mm, "mid": v(31.38, 16.14) * mm, "end": v(31.75, 15.24) * mm});
            skArc(sketch, "E145.MirrorCS", {"start": v(19.05, 30.48) * mm, "mid": v(19.42, 31.38) * mm, "end": v(20.32, 31.75) * mm});
            skArc(sketch, "E146.MirrorCS", {"start": v(-19.05, 45.72) * mm, "mid": v(-19.42, 46.62) * mm, "end": v(-20.32, 47) * mm});
            skArc(sketch, "E147.MirrorCS", {"start": v(-5.08, 3.81) * mm, "mid": v(-4.18, 4.18) * mm, "end": v(-3.81, 5.08) * mm});
            skArc(sketch, "E148.MirrorCS", {"start": v(-3.81, 30.48) * mm, "mid": v(-4.18, 31.38) * mm, "end": v(-5.08, 31.75) * mm});
            skArc(sketch, "E149.MirrorCS", {"start": v(5.08, 19.05) * mm, "mid": v(4.18, 19.42) * mm, "end": v(3.81, 20.32) * mm});
            skArc(sketch, "E150.MirrorCS", {"start": v(31.75, 35.56) * mm, "mid": v(31.38, 34.66) * mm, "end": v(30.48, 34.3) * mm});
            skArc(sketch, "E151.MirrorCS", {"start": v(16.51, 20.32) * mm, "mid": v(16.14, 19.42) * mm, "end": v(15.24, 19.05) * mm});
            skArc(sketch, "E152.MirrorCS", {"start": v(-5.08, 34.3) * mm, "mid": v(-4.18, 34.66) * mm, "end": v(-3.81, 35.56) * mm});
            skArc(sketch, "E153.MirrorCS", {"start": v(-47, 5.08) * mm, "mid": v(-46.62, 4.18) * mm, "end": v(-45.72, 3.81) * mm});
            skArc(sketch, "E154.MirrorCS", {"start": v(31.75, 5.08) * mm, "mid": v(31.38, 4.18) * mm, "end": v(30.48, 3.81) * mm});
            skArc(sketch, "E155.MirrorCS", {"start": v(47, 5.08) * mm, "mid": v(46.62, 4.18) * mm, "end": v(45.72, 3.81) * mm});
            skArc(sketch, "E156.MirrorCS", {"start": v(31.75, 20.32) * mm, "mid": v(31.38, 19.42) * mm, "end": v(30.48, 19.05) * mm});
            skArc(sketch, "E157.MirrorCS", {"start": v(20.32, 34.3) * mm, "mid": v(19.42, 34.66) * mm, "end": v(19.05, 35.56) * mm});
            skArc(sketch, "E158.MirrorCS", {"start": v(-30.48, 16.51) * mm, "mid": v(-31.38, 16.14) * mm, "end": v(-31.75, 15.24) * mm});
            skArc(sketch, "E159.MirrorCS", {"start": v(20.32, 3.81) * mm, "mid": v(19.42, 4.18) * mm, "end": v(19.05, 5.08) * mm});
            skArc(sketch, "E160.MirrorCS", {"start": v(16.51, 5.08) * mm, "mid": v(16.14, 4.18) * mm, "end": v(15.24, 3.81) * mm});
            skArc(sketch, "E161.MirrorCS", {"start": v(-47, 20.32) * mm, "mid": v(-46.62, 19.42) * mm, "end": v(-45.72, 19.05) * mm});
            skArc(sketch, "E162.MirrorCS", {"start": v(47, 20.32) * mm, "mid": v(46.62, 19.42) * mm, "end": v(45.72, 19.05) * mm});
            skArc(sketch, "E163.MirrorCS", {"start": v(-3.81, 45.72) * mm, "mid": v(-4.18, 46.62) * mm, "end": v(-5.08, 47) * mm});
            skLineSegment(sketch, "E164.MirrorCS", {"start": v(-35.56, 34.3) * mm, "end": v(-45.72, 34.3) * mm});
            skLineSegment(sketch, "E165.MirrorCS", {"start": v(-31.75, 5.08) * mm, "end": v(-31.75, 15.24) * mm});
            skLineSegment(sketch, "E166.MirrorCS", {"start": v(5.08, 19.05) * mm, "end": v(15.24, 19.05) * mm});
            skLineSegment(sketch, "E167.MirrorCS", {"start": v(35.56, 19.05) * mm, "end": v(45.72, 19.05) * mm});
            skLineSegment(sketch, "E168.MirrorCS", {"start": v(20.32, 34.3) * mm, "end": v(30.48, 34.3) * mm});
            skLineSegment(sketch, "E169.MirrorCS", {"start": v(20.32, 3.81) * mm, "end": v(30.48, 3.81) * mm});
            skLineSegment(sketch, "E170.MirrorCS", {"start": v(-3.81, 20.32) * mm, "end": v(-3.81, 30.48) * mm});
            skLineSegment(sketch, "E171.MirrorCS", {"start": v(-3.81, 35.56) * mm, "end": v(-3.81, 45.72) * mm});
            skLineSegment(sketch, "E172.MirrorCS", {"start": v(-20.32, 19.05) * mm, "end": v(-30.48, 19.05) * mm});
            skLineSegment(sketch, "E173.MirrorCS", {"start": v(-16.51, 20.32) * mm, "end": v(-16.51, 30.48) * mm});
            skLineSegment(sketch, "E174.MirrorCS", {"start": v(3.81, 20.32) * mm, "end": v(3.8, 30.48) * mm});
            skLineSegment(sketch, "E175.MirrorCS", {"start": v(36.51, 44.77) * mm, "end": v(21.27, 44.77) * mm, "construction": true});
            skLineSegment(sketch, "E176.MirrorCS", {"start": v(-35.56, 19.05) * mm, "end": v(-45.72, 19.05) * mm});
            skLineSegment(sketch, "E177.MirrorCS", {"start": v(19.05, 35.56) * mm, "end": v(19.05, 45.72) * mm});
            skLineSegment(sketch, "E178.MirrorCS", {"start": v(19.05, 5.08) * mm, "end": v(19.05, 15.24) * mm});
            skPoint(sketch, "E179.MirrorP", {"position": v(34.29, 34.3) * mm});
            skLineSegment(sketch, "E180.MirrorCS", {"start": v(-46.99, 35.56) * mm, "end": v(-46.99, 45.72) * mm});
            skLineSegment(sketch, "E181.MirrorCS", {"start": v(-31.75, 20.32) * mm, "end": v(-31.75, 30.48) * mm});
            skLineSegment(sketch, "E182.MirrorCS", {"start": v(-5.08, 16.51) * mm, "end": v(-15.24, 16.51) * mm});
            skLineSegment(sketch, "E183.MirrorCS", {"start": v(31.75, 20.32) * mm, "end": v(31.75, 30.48) * mm});
            skLineSegment(sketch, "E184.MirrorCS", {"start": v(16.51, 35.56) * mm, "end": v(16.5, 45.72) * mm});
            skLineSegment(sketch, "E185.MirrorCS", {"start": v(16.51, 5.08) * mm, "end": v(16.51, 15.24) * mm});
            skLineSegment(sketch, "E186.MirrorCS", {"start": v(47, 5.08) * mm, "end": v(47, 15.24) * mm});
            skLineSegment(sketch, "E187.MirrorCS", {"start": v(-20.32, 47) * mm, "end": v(-30.48, 47) * mm});
            skLineSegment(sketch, "E188.MirrorCS", {"start": v(-34.3, 20.32) * mm, "end": v(-34.3, 30.48) * mm});
            skPoint(sketch, "E189.MirrorP", {"position": v(-46.99, 47) * mm});
            skLineSegment(sketch, "E190.MirrorCS", {"start": v(16.51, 20.32) * mm, "end": v(16.51, 30.48) * mm});
            skLineSegment(sketch, "E191.MirrorCS", {"start": v(47, 20.32) * mm, "end": v(46.99, 30.48) * mm});
            skLineSegment(sketch, "E192.MirrorCS", {"start": v(31.75, 35.56) * mm, "end": v(31.75, 45.72) * mm});
            skLineSegment(sketch, "E193.MirrorCS", {"start": v(31.75, 5.08) * mm, "end": v(31.75, 15.24) * mm});
            skPoint(sketch, "E194.MirrorP", {"position": v(-40.64, 40.64) * mm});
            skLineSegment(sketch, "E195.MirrorCS", {"start": v(-20.32, 16.51) * mm, "end": v(-30.48, 16.51) * mm});
            skLineSegment(sketch, "E196.MirrorCS", {"start": v(-19.05, 20.32) * mm, "end": v(-19.05, 30.48) * mm});
            skLineSegment(sketch, "E197.MirrorCS", {"start": v(-35.56, 31.75) * mm, "end": v(-45.72, 31.75) * mm});
            skLineSegment(sketch, "E198.MirrorCS", {"start": v(-5.08, 3.81) * mm, "end": v(-15.24, 3.81) * mm});
            skPoint(sketch, "E199.MirrorP", {"position": v(46.99, 47) * mm});
            skLineSegment(sketch, "E200.MirrorCS", {"start": v(-5.08, 19.05) * mm, "end": v(-15.24, 19.05) * mm});
            skLineSegment(sketch, "E201.MirrorCS", {"start": v(-20.32, 3.81) * mm, "end": v(-30.48, 3.81) * mm});
            skLineSegment(sketch, "E202.MirrorCS", {"start": v(-34.3, 5.08) * mm, "end": v(-34.3, 15.24) * mm});
            skLineSegment(sketch, "E203.MirrorCS", {"start": v(-5.08, 34.3) * mm, "end": v(-15.24, 34.3) * mm});
            skLineSegment(sketch, "E204.MirrorCS", {"start": v(20.32, 31.75) * mm, "end": v(30.48, 31.75) * mm});
            skLineSegment(sketch, "E205.MirrorCS", {"start": v(5.08, 47) * mm, "end": v(15.24, 47) * mm});
            skLineSegment(sketch, "E206.MirrorCS", {"start": v(5.08, 16.51) * mm, "end": v(15.24, 16.51) * mm});
            skLineSegment(sketch, "E207.MirrorCS", {"start": v(20.32, 19.05) * mm, "end": v(30.48, 19.05) * mm});
            skLineSegment(sketch, "E208.MirrorCS", {"start": v(-20.32, 34.3) * mm, "end": v(-30.48, 34.3) * mm});
            skLineSegment(sketch, "E209.MirrorCS", {"start": v(20.32, 16.51) * mm, "end": v(30.48, 16.51) * mm});
            skLineSegment(sketch, "E210.MirrorCS", {"start": v(-47, 5.08) * mm, "end": v(-47, 15.24) * mm});
            skLineSegment(sketch, "E211.MirrorCS", {"start": v(-36.51, 44.77) * mm, "end": v(-36.51, 29.53) * mm, "construction": true});
            skLineSegment(sketch, "E212.MirrorCS", {"start": v(20.32, 47) * mm, "end": v(30.48, 47) * mm});
            skPoint(sketch, "E213.MirrorP", {"position": v(-46.99, 34.3) * mm});
            skLineSegment(sketch, "E214.MirrorCS", {"start": v(-3.81, 5.08) * mm, "end": v(-3.81, 15.24) * mm});
            skLineSegment(sketch, "E215.MirrorCS", {"start": v(46.99, 35.56) * mm, "end": v(46.99, 45.72) * mm});
            skLineSegment(sketch, "E216.MirrorCS", {"start": v(34.3, 5.08) * mm, "end": v(34.3, 15.24) * mm});
            skLineSegment(sketch, "E217.MirrorCS", {"start": v(-20.32, 31.75) * mm, "end": v(-30.48, 31.75) * mm});
            skPoint(sketch, "E218.MirrorP", {"position": v(-34.3, 47) * mm});
            skLineSegment(sketch, "E219.MirrorCS", {"start": v(34.29, 35.56) * mm, "end": v(34.29, 45.72) * mm});
            skLineSegment(sketch, "E220.MirrorCS", {"start": v(35.56, 3.81) * mm, "end": v(45.72, 3.81) * mm});
            skLineSegment(sketch, "E221.MirrorCS", {"start": v(-19.05, 35.56) * mm, "end": v(-19.05, 45.72) * mm});
            skPoint(sketch, "E222.MirrorP", {"position": v(46.99, 34.3) * mm});
            skLineSegment(sketch, "E223.MirrorCS", {"start": v(35.56, 47) * mm, "end": v(45.72, 47) * mm});
            skLineSegment(sketch, "E224.MirrorCS", {"start": v(5.08, 3.81) * mm, "end": v(15.24, 3.81) * mm});
            skLineSegment(sketch, "E225.MirrorCS", {"start": v(3.81, 5.08) * mm, "end": v(3.81, 15.24) * mm});
            skLineSegment(sketch, "E226.MirrorCS", {"start": v(34.3, 20.32) * mm, "end": v(34.29, 30.48) * mm});
            skLineSegment(sketch, "E227.MirrorCS", {"start": v(-35.56, 3.81) * mm, "end": v(-45.72, 3.81) * mm});
            skLineSegment(sketch, "E228.MirrorCS", {"start": v(-31.75, 35.56) * mm, "end": v(-31.75, 45.72) * mm});
            skPoint(sketch, "E229.MirrorP", {"position": v(34.29, 47) * mm});
            skLineSegment(sketch, "E230.MirrorCS", {"start": v(-19.05, 5.08) * mm, "end": v(-19.05, 15.24) * mm});
            skLineSegment(sketch, "E231.MirrorCS", {"start": v(5.08, 31.75) * mm, "end": v(15.24, 31.75) * mm});
            skLineSegment(sketch, "E232.MirrorCS", {"start": v(36.51, 44.77) * mm, "end": v(36.51, 29.53) * mm, "construction": true});
            skLineSegment(sketch, "E233.MirrorCS", {"start": v(-5.08, 31.75) * mm, "end": v(-15.24, 31.75) * mm});
            skPoint(sketch, "E234.MirrorP", {"position": v(-34.29, 34.3) * mm});
            skLineSegment(sketch, "E235.MirrorCS", {"start": v(-36.51, 44.77) * mm, "end": v(-21.27, 44.77) * mm, "construction": true});
            skLineSegment(sketch, "E236.MirrorCS", {"start": v(35.56, 31.75) * mm, "end": v(45.72, 31.75) * mm});
            skLineSegment(sketch, "E237.MirrorCS", {"start": v(19.05, 20.32) * mm, "end": v(19.05, 30.48) * mm});
            skLineSegment(sketch, "E238.MirrorCS", {"start": v(-35.56, 16.51) * mm, "end": v(-45.72, 16.51) * mm});
            skLineSegment(sketch, "E239.MirrorCS", {"start": v(35.56, 34.3) * mm, "end": v(45.72, 34.3) * mm});
            skLineSegment(sketch, "E240.MirrorCS", {"start": v(-16.51, 35.56) * mm, "end": v(-16.51, 45.72) * mm});
            skLineSegment(sketch, "E241.MirrorCS", {"start": v(35.56, 16.51) * mm, "end": v(45.72, 16.51) * mm});
            skLineSegment(sketch, "E242.MirrorCS", {"start": v(-34.29, 35.56) * mm, "end": v(-34.29, 45.72) * mm});
            skLineSegment(sketch, "E243.MirrorCS", {"start": v(-5.08, 47) * mm, "end": v(-15.24, 47) * mm});
            skLineSegment(sketch, "E244.MirrorCS", {"start": v(3.81, 35.56) * mm, "end": v(3.8, 45.72) * mm});
            skLineSegment(sketch, "E245.MirrorCS", {"start": v(-16.51, 5.08) * mm, "end": v(-16.51, 15.24) * mm});
            skLineSegment(sketch, "E246.MirrorCS", {"start": v(5.08, 34.3) * mm, "end": v(15.24, 34.3) * mm});
            skLineSegment(sketch, "E247.MirrorCS", {"start": v(-47, 20.32) * mm, "end": v(-47, 30.48) * mm});
            skPoint(sketch, "E248.MirrorP", {"position": v(40.64, 40.64) * mm});
            skLineSegment(sketch, "E249.MirrorCS", {"start": v(-35.56, 47) * mm, "end": v(-45.72, 47) * mm});
            skSolve(sketch);
        }
        {
            var Q0;
            Q0=qSketchRegion(id+"F0",true);
            extrude(context, id + "F1", {"entities" : qUnion([Q0]), "depth" : 2.54 * mm, "offsetDistance" : 25.4 * mm});
        }
        {
            var Q0;
            Q0=makeQuery(id+"F1.opExtrude","CAP_FACE",FACE,{"disambiguationData":[OSD([sQuery(id+"F0.wireOp",EDGE,"E0.bottom"),sQuery(id+"F0.wireOp",EDGE,"E0.top"),sQuery(id+"F0.wireOp",EDGE,"E0.left"),sQuery(id+"F0.wireOp",EDGE,"E0.right"),sQuery(id+"F0.wireOp",EDGE,"E1"),sQuery(id+"F0.wireOp",EDGE,"E4.MirrorC"),sQuery(id+"F0.wireOp",EDGE,"E5.MirrorC"),sQuery(id+"F0.wireOp",EDGE,"E6.MirrorC"),sQuery(id+"F0.wireOp",EDGE,"E7.bottom"),sQuery(id+"F0.wireOp",EDGE,"E7.top"),sQuery(id+"F0.wireOp",EDGE,"E7.left"),sQuery(id+"F0.wireOp",EDGE,"E7.right"),sQuery(id+"F0.wireOp",EDGE,"E8.filletArc"),sQuery(id+"F0.wireOp",EDGE,"E9.filletArc"),sQuery(id+"F0.wireOp",EDGE,"E10.filletArc"),sQuery(id+"F0.wireOp",EDGE,"E11.filletArc"),sQuery(id+"F0.wireOp",EDGE,"E12.0.1.0"),sQuery(id+"F0.wireOp",EDGE,"E12.0.1.1"),sQuery(id+"F0.wireOp",EDGE,"E12.0.1.2"),sQuery(id+"F0.wireOp",EDGE,"E12.0.1.3"),sQuery(id+"F0.wireOp",EDGE,"E12.0.1.4"),sQuery(id+"F0.wireOp",EDGE,"E12.0.1.5"),sQuery(id+"F0.wireOp",EDGE,"E12.0.1.6"),sQuery(id+"F0.wireOp",EDGE,"E12.0.1.7"),sQuery(id+"F0.wireOp",EDGE,"E12.0.2.0"),sQuery(id+"F0.wireOp",EDGE,"E12.0.2.1"),sQuery(id+"F0.wireOp",EDGE,"E12.0.2.2"),sQuery(id+"F0.wireOp",EDGE,"E12.0.2.3"),sQuery(id+"F0.wireOp",EDGE,"E12.0.2.4"),sQuery(id+"F0.wireOp",EDGE,"E12.0.2.5"),sQuery(id+"F0.wireOp",EDGE,"E12.0.2.6"),sQuery(id+"F0.wireOp",EDGE,"E12.0.2.7"),sQuery(id+"F0.wireOp",EDGE,"E12.1.0.0"),sQuery(id+"F0.wireOp",EDGE,"E12.1.0.1"),sQuery(id+"F0.wireOp",EDGE,"E12.1.0.2"),sQuery(id+"F0.wireOp",EDGE,"E12.1.0.3"),sQuery(id+"F0.wireOp",EDGE,"E12.1.0.4"),sQuery(id+"F0.wireOp",EDGE,"E12.1.0.5"),sQuery(id+"F0.wireOp",EDGE,"E12.1.0.6"),sQuery(id+"F0.wireOp",EDGE,"E12.1.0.7"),sQuery(id+"F0.wireOp",EDGE,"E12.1.1.0"),sQuery(id+"F0.wireOp",EDGE,"E12.1.1.1"),sQuery(id+"F0.wireOp",EDGE,"E12.1.1.2"),sQuery(id+"F0.wireOp",EDGE,"E12.1.1.3"),sQuery(id+"F0.wireOp",EDGE,"E12.1.1.4"),sQuery(id+"F0.wireOp",EDGE,"E12.1.1.5"),sQuery(id+"F0.wireOp",EDGE,"E12.1.1.6"),sQuery(id+"F0.wireOp",EDGE,"E12.1.1.7"),sQuery(id+"F0.wireOp",EDGE,"E12.1.2.0"),sQuery(id+"F0.wireOp",EDGE,"E12.1.2.1"),sQuery(id+"F0.wireOp",EDGE,"E12.1.2.2"),sQuery(id+"F0.wireOp",EDGE,"E12.1.2.3"),sQuery(id+"F0.wireOp",EDGE,"E12.1.2.4"),sQuery(id+"F0.wireOp",EDGE,"E12.1.2.5"),sQuery(id+"F0.wireOp",EDGE,"E12.1.2.6"),sQuery(id+"F0.wireOp",EDGE,"E12.1.2.7"),sQuery(id+"F0.wireOp",EDGE,"E12.2.0.0"),sQuery(id+"F0.wireOp",EDGE,"E12.2.0.1"),sQuery(id+"F0.wireOp",EDGE,"E12.2.0.2"),sQuery(id+"F0.wireOp",EDGE,"E12.2.0.3"),sQuery(id+"F0.wireOp",EDGE,"E12.2.0.4"),sQuery(id+"F0.wireOp",EDGE,"E12.2.0.5"),sQuery(id+"F0.wireOp",EDGE,"E12.2.0.6"),sQuery(id+"F0.wireOp",EDGE,"E12.2.0.7"),sQuery(id+"F0.wireOp",EDGE,"E12.2.1.0"),sQuery(id+"F0.wireOp",EDGE,"E12.2.1.1"),sQuery(id+"F0.wireOp",EDGE,"E12.2.1.2"),sQuery(id+"F0.wireOp",EDGE,"E12.2.1.3"),sQuery(id+"F0.wireOp",EDGE,"E12.2.1.4"),sQuery(id+"F0.wireOp",EDGE,"E12.2.1.5"),sQuery(id+"F0.wireOp",EDGE,"E12.2.1.6"),sQuery(id+"F0.wireOp",EDGE,"E12.2.1.7"),sQuery(id+"F0.wireOp",EDGE,"E12.2.2.0"),sQuery(id+"F0.wireOp",EDGE,"E12.2.2.1"),sQuery(id+"F0.wireOp",EDGE,"E12.2.2.2"),sQuery(id+"F0.wireOp",EDGE,"E12.2.2.3"),sQuery(id+"F0.wireOp",EDGE,"E12.2.2.4"),sQuery(id+"F0.wireOp",EDGE,"E12.2.2.5"),sQuery(id+"F0.wireOp",EDGE,"E12.2.2.6"),sQuery(id+"F0.wireOp",EDGE,"E12.2.2.7"),sQuery(id+"F0.wireOp",EDGE,"E13.MirrorCS"),sQuery(id+"F0.wireOp",EDGE,"E14.MirrorCS"),sQuery(id+"F0.wireOp",EDGE,"E15.MirrorCS"),sQuery(id+"F0.wireOp",EDGE,"E16.MirrorCS"),sQuery(id+"F0.wireOp",EDGE,"E17.MirrorCS"),sQuery(id+"F0.wireOp",EDGE,"E18.MirrorCS"),sQuery(id+"F0.wireOp",EDGE,"E19.MirrorCS"),sQuery(id+"F0.wireOp",EDGE,"E20.MirrorCS"),sQuery(id+"F0.wireOp",EDGE,"E21.MirrorCS"),sQuery(id+"F0.wireOp",EDGE,"E22.MirrorCS"),sQuery(id+"F0.wireOp",EDGE,"E23.MirrorCS"),sQuery(id+"F0.wireOp",EDGE,"E24.MirrorCS"),sQuery(id+"F0.wireOp",EDGE,"E25.MirrorCS"),sQuery(id+"F0.wireOp",EDGE,"E26.MirrorCS"),sQuery(id+"F0.wireOp",EDGE,"E27.MirrorCS"),sQuery(id+"F0.wireOp",EDGE,"E28.MirrorCS"),sQuery(id+"F0.wireOp",EDGE,"E29.MirrorCS"),sQuery(id+"F0.wireOp",EDGE,"E30.MirrorCS"),sQuery(id+"F0.wireOp",EDGE,"E31.MirrorCS"),sQuery(id+"F0.wireOp",EDGE,"E32.MirrorCS"),sQuery(id+"F0.wireOp",EDGE,"E33.MirrorCS"),sQuery(id+"F0.wireOp",EDGE,"E34.MirrorCS"),sQuery(id+"F0.wireOp",EDGE,"E35.MirrorCS"),sQuery(id+"F0.wireOp",EDGE,"E36.MirrorCS"),sQuery(id+"F0.wireOp",EDGE,"E37.MirrorCS"),sQuery(id+"F0.wireOp",EDGE,"E38.MirrorCS"),sQuery(id+"F0.wireOp",EDGE,"E39.MirrorCS"),sQuery(id+"F0.wireOp",EDGE,"E40.MirrorCS"),sQuery(id+"F0.wireOp",EDGE,"E41.MirrorCS"),sQuery(id+"F0.wireOp",EDGE,"E42.MirrorCS"),sQuery(id+"F0.wireOp",EDGE,"E43.MirrorCS"),sQuery(id+"F0.wireOp",EDGE,"E44.MirrorCS"),sQuery(id+"F0.wireOp",EDGE,"E45.MirrorCS"),sQuery(id+"F0.wireOp",EDGE,"E46.MirrorCS"),sQuery(id+"F0.wireOp",EDGE,"E47.MirrorCS"),sQuery(id+"F0.wireOp",EDGE,"E48.MirrorCS"),sQuery(id+"F0.wireOp",EDGE,"E49.MirrorCS"),sQuery(id+"F0.wireOp",EDGE,"E50.MirrorCS"),sQuery(id+"F0.wireOp",EDGE,"E51.MirrorCS"),sQuery(id+"F0.wireOp",EDGE,"E52.MirrorCS"),sQuery(id+"F0.wireOp",EDGE,"E53.MirrorCS"),sQuery(id+"F0.wireOp",EDGE,"E54.MirrorCS"),sQuery(id+"F0.wireOp",EDGE,"E56.MirrorCS"),sQuery(id+"F0.wireOp",EDGE,"E57.MirrorCS"),sQuery(id+"F0.wireOp",EDGE,"E58.MirrorCS"),sQuery(id+"F0.wireOp",EDGE,"E59.MirrorCS"),sQuery(id+"F0.wireOp",EDGE,"E60.MirrorCS"),sQuery(id+"F0.wireOp",EDGE,"E63.MirrorCS"),sQuery(id+"F0.wireOp",EDGE,"E64.MirrorCS"),sQuery(id+"F0.wireOp",EDGE,"E65.MirrorCS"),sQuery(id+"F0.wireOp",EDGE,"E66.MirrorCS"),sQuery(id+"F0.wireOp",EDGE,"E67.MirrorCS"),sQuery(id+"F0.wireOp",EDGE,"E68.MirrorCS"),sQuery(id+"F0.wireOp",EDGE,"E69.MirrorCS"),sQuery(id+"F0.wireOp",EDGE,"E70.MirrorCS"),sQuery(id+"F0.wireOp",EDGE,"E71.MirrorCS"),sQuery(id+"F0.wireOp",EDGE,"E72.MirrorCS"),sQuery(id+"F0.wireOp",EDGE,"E73.MirrorCS"),sQuery(id+"F0.wireOp",EDGE,"E76.MirrorCS"),sQuery(id+"F0.wireOp",EDGE,"E77.MirrorCS"),sQuery(id+"F0.wireOp",EDGE,"E78.MirrorCS"),sQuery(id+"F0.wireOp",EDGE,"E80.MirrorCS"),sQuery(id+"F0.wireOp",EDGE,"E81.MirrorCS"),sQuery(id+"F0.wireOp",EDGE,"E82.MirrorCS"),sQuery(id+"F0.wireOp",EDGE,"E84.MirrorCS"),sQuery(id+"F0.wireOp",EDGE,"E85.MirrorCS"),sQuery(id+"F0.wireOp",EDGE,"E86.MirrorCS"),sQuery(id+"F0.wireOp",EDGE,"E87.MirrorCS"),sQuery(id+"F0.wireOp",EDGE,"E88.MirrorCS"),sQuery(id+"F0.wireOp",EDGE,"E89.MirrorCS"),sQuery(id+"F0.wireOp",EDGE,"E90.MirrorCS"),sQuery(id+"F0.wireOp",EDGE,"E91.MirrorCS"),sQuery(id+"F0.wireOp",EDGE,"E92.MirrorCS"),sQuery(id+"F0.wireOp",EDGE,"E93.MirrorCS"),sQuery(id+"F0.wireOp",EDGE,"E94.MirrorCS"),sQuery(id+"F0.wireOp",EDGE,"E95.MirrorCS"),sQuery(id+"F0.wireOp",EDGE,"E96.MirrorCS"),sQuery(id+"F0.wireOp",EDGE,"E97.MirrorCS"),sQuery(id+"F0.wireOp",EDGE,"E98.MirrorCS"),sQuery(id+"F0.wireOp",EDGE,"E99.MirrorCS"),sQuery(id+"F0.wireOp",EDGE,"E100.MirrorCS"),sQuery(id+"F0.wireOp",EDGE,"E101.MirrorCS"),sQuery(id+"F0.wireOp",EDGE,"E102.MirrorCS"),sQuery(id+"F0.wireOp",EDGE,"E103.MirrorCS"),sQuery(id+"F0.wireOp",EDGE,"E104.MirrorCS"),sQuery(id+"F0.wireOp",EDGE,"E105.MirrorCS"),sQuery(id+"F0.wireOp",EDGE,"E106.MirrorCS"),sQuery(id+"F0.wireOp",EDGE,"E107.MirrorCS"),sQuery(id+"F0.wireOp",EDGE,"E108.MirrorCS"),sQuery(id+"F0.wireOp",EDGE,"E109.MirrorCS"),sQuery(id+"F0.wireOp",EDGE,"E110.MirrorCS"),sQuery(id+"F0.wireOp",EDGE,"E111.MirrorCS"),sQuery(id+"F0.wireOp",EDGE,"E112.MirrorCS"),sQuery(id+"F0.wireOp",EDGE,"E113.MirrorCS"),sQuery(id+"F0.wireOp",EDGE,"E114.MirrorCS"),sQuery(id+"F0.wireOp",EDGE,"E115.MirrorCS"),sQuery(id+"F0.wireOp",EDGE,"E116.MirrorCS"),sQuery(id+"F0.wireOp",EDGE,"E117.MirrorCS"),sQuery(id+"F0.wireOp",EDGE,"E118.MirrorCS"),sQuery(id+"F0.wireOp",EDGE,"E119.MirrorCS"),sQuery(id+"F0.wireOp",EDGE,"E120.MirrorCS"),sQuery(id+"F0.wireOp",EDGE,"E121.MirrorCS"),sQuery(id+"F0.wireOp",EDGE,"E122.MirrorCS"),sQuery(id+"F0.wireOp",EDGE,"E123.MirrorCS"),sQuery(id+"F0.wireOp",EDGE,"E124.MirrorCS"),sQuery(id+"F0.wireOp",EDGE,"E125.MirrorCS"),sQuery(id+"F0.wireOp",EDGE,"E126.MirrorCS"),sQuery(id+"F0.wireOp",EDGE,"E127.MirrorCS"),sQuery(id+"F0.wireOp",EDGE,"E128.MirrorCS"),sQuery(id+"F0.wireOp",EDGE,"E129.MirrorCS"),sQuery(id+"F0.wireOp",EDGE,"E130.MirrorCS"),sQuery(id+"F0.wireOp",EDGE,"E131.MirrorCS"),sQuery(id+"F0.wireOp",EDGE,"E132.MirrorCS"),sQuery(id+"F0.wireOp",EDGE,"E133.MirrorCS"),sQuery(id+"F0.wireOp",EDGE,"E134.MirrorCS"),sQuery(id+"F0.wireOp",EDGE,"E135.MirrorCS"),sQuery(id+"F0.wireOp",EDGE,"E136.MirrorCS"),sQuery(id+"F0.wireOp",EDGE,"E137.MirrorCS"),sQuery(id+"F0.wireOp",EDGE,"E138.MirrorCS"),sQuery(id+"F0.wireOp",EDGE,"E139.MirrorCS"),sQuery(id+"F0.wireOp",EDGE,"E140.MirrorCS"),sQuery(id+"F0.wireOp",EDGE,"E141.MirrorCS"),sQuery(id+"F0.wireOp",EDGE,"E142.MirrorCS"),sQuery(id+"F0.wireOp",EDGE,"E143.MirrorCS"),sQuery(id+"F0.wireOp",EDGE,"E144.MirrorCS"),sQuery(id+"F0.wireOp",EDGE,"E145.MirrorCS"),sQuery(id+"F0.wireOp",EDGE,"E146.MirrorCS"),sQuery(id+"F0.wireOp",EDGE,"E147.MirrorCS"),sQuery(id+"F0.wireOp",EDGE,"E148.MirrorCS"),sQuery(id+"F0.wireOp",EDGE,"E149.MirrorCS"),sQuery(id+"F0.wireOp",EDGE,"E150.MirrorCS"),sQuery(id+"F0.wireOp",EDGE,"E151.MirrorCS"),sQuery(id+"F0.wireOp",EDGE,"E152.MirrorCS"),sQuery(id+"F0.wireOp",EDGE,"E153.MirrorCS"),sQuery(id+"F0.wireOp",EDGE,"E154.MirrorCS"),sQuery(id+"F0.wireOp",EDGE,"E155.MirrorCS"),sQuery(id+"F0.wireOp",EDGE,"E156.MirrorCS"),sQuery(id+"F0.wireOp",EDGE,"E157.MirrorCS"),sQuery(id+"F0.wireOp",EDGE,"E158.MirrorCS"),sQuery(id+"F0.wireOp",EDGE,"E159.MirrorCS"),sQuery(id+"F0.wireOp",EDGE,"E160.MirrorCS"),sQuery(id+"F0.wireOp",EDGE,"E161.MirrorCS"),sQuery(id+"F0.wireOp",EDGE,"E162.MirrorCS"),sQuery(id+"F0.wireOp",EDGE,"E163.MirrorCS"),sQuery(id+"F0.wireOp",EDGE,"E164.MirrorCS"),sQuery(id+"F0.wireOp",EDGE,"E165.MirrorCS"),sQuery(id+"F0.wireOp",EDGE,"E166.MirrorCS"),sQuery(id+"F0.wireOp",EDGE,"E167.MirrorCS"),sQuery(id+"F0.wireOp",EDGE,"E168.MirrorCS"),sQuery(id+"F0.wireOp",EDGE,"E169.MirrorCS"),sQuery(id+"F0.wireOp",EDGE,"E170.MirrorCS"),sQuery(id+"F0.wireOp",EDGE,"E171.MirrorCS"),sQuery(id+"F0.wireOp",EDGE,"E172.MirrorCS"),sQuery(id+"F0.wireOp",EDGE,"E173.MirrorCS"),sQuery(id+"F0.wireOp",EDGE,"E174.MirrorCS"),sQuery(id+"F0.wireOp",EDGE,"E176.MirrorCS"),sQuery(id+"F0.wireOp",EDGE,"E177.MirrorCS"),sQuery(id+"F0.wireOp",EDGE,"E178.MirrorCS"),sQuery(id+"F0.wireOp",EDGE,"E180.MirrorCS"),sQuery(id+"F0.wireOp",EDGE,"E181.MirrorCS"),sQuery(id+"F0.wireOp",EDGE,"E182.MirrorCS"),sQuery(id+"F0.wireOp",EDGE,"E183.MirrorCS"),sQuery(id+"F0.wireOp",EDGE,"E184.MirrorCS"),sQuery(id+"F0.wireOp",EDGE,"E185.MirrorCS"),sQuery(id+"F0.wireOp",EDGE,"E186.MirrorCS"),sQuery(id+"F0.wireOp",EDGE,"E187.MirrorCS"),sQuery(id+"F0.wireOp",EDGE,"E188.MirrorCS"),sQuery(id+"F0.wireOp",EDGE,"E190.MirrorCS"),sQuery(id+"F0.wireOp",EDGE,"E191.MirrorCS"),sQuery(id+"F0.wireOp",EDGE,"E192.MirrorCS"),sQuery(id+"F0.wireOp",EDGE,"E193.MirrorCS"),sQuery(id+"F0.wireOp",EDGE,"E195.MirrorCS"),sQuery(id+"F0.wireOp",EDGE,"E196.MirrorCS"),sQuery(id+"F0.wireOp",EDGE,"E197.MirrorCS"),sQuery(id+"F0.wireOp",EDGE,"E198.MirrorCS"),sQuery(id+"F0.wireOp",EDGE,"E200.MirrorCS"),sQuery(id+"F0.wireOp",EDGE,"E201.MirrorCS"),sQuery(id+"F0.wireOp",EDGE,"E202.MirrorCS"),sQuery(id+"F0.wireOp",EDGE,"E203.MirrorCS"),sQuery(id+"F0.wireOp",EDGE,"E204.MirrorCS"),sQuery(id+"F0.wireOp",EDGE,"E205.MirrorCS"),sQuery(id+"F0.wireOp",EDGE,"E206.MirrorCS"),sQuery(id+"F0.wireOp",EDGE,"E207.MirrorCS"),sQuery(id+"F0.wireOp",EDGE,"E208.MirrorCS"),sQuery(id+"F0.wireOp",EDGE,"E209.MirrorCS"),sQuery(id+"F0.wireOp",EDGE,"E210.MirrorCS"),sQuery(id+"F0.wireOp",EDGE,"E212.MirrorCS"),sQuery(id+"F0.wireOp",EDGE,"E214.MirrorCS"),sQuery(id+"F0.wireOp",EDGE,"E215.MirrorCS"),sQuery(id+"F0.wireOp",EDGE,"E216.MirrorCS"),sQuery(id+"F0.wireOp",EDGE,"E217.MirrorCS"),sQuery(id+"F0.wireOp",EDGE,"E219.MirrorCS"),sQuery(id+"F0.wireOp",EDGE,"E220.MirrorCS"),sQuery(id+"F0.wireOp",EDGE,"E221.MirrorCS"),sQuery(id+"F0.wireOp",EDGE,"E223.MirrorCS"),sQuery(id+"F0.wireOp",EDGE,"E224.MirrorCS"),sQuery(id+"F0.wireOp",EDGE,"E225.MirrorCS"),sQuery(id+"F0.wireOp",EDGE,"E226.MirrorCS"),sQuery(id+"F0.wireOp",EDGE,"E227.MirrorCS"),sQuery(id+"F0.wireOp",EDGE,"E228.MirrorCS"),sQuery(id+"F0.wireOp",EDGE,"E230.MirrorCS"),sQuery(id+"F0.wireOp",EDGE,"E231.MirrorCS"),sQuery(id+"F0.wireOp",EDGE,"E233.MirrorCS"),sQuery(id+"F0.wireOp",EDGE,"E236.MirrorCS"),sQuery(id+"F0.wireOp",EDGE,"E237.MirrorCS"),sQuery(id+"F0.wireOp",EDGE,"E238.MirrorCS"),sQuery(id+"F0.wireOp",EDGE,"E239.MirrorCS"),sQuery(id+"F0.wireOp",EDGE,"E240.MirrorCS"),sQuery(id+"F0.wireOp",EDGE,"E241.MirrorCS"),sQuery(id+"F0.wireOp",EDGE,"E242.MirrorCS"),sQuery(id+"F0.wireOp",EDGE,"E243.MirrorCS"),sQuery(id+"F0.wireOp",EDGE,"E244.MirrorCS"),sQuery(id+"F0.wireOp",EDGE,"E245.MirrorCS"),sQuery(id+"F0.wireOp",EDGE,"E246.MirrorCS"),sQuery(id+"F0.wireOp",EDGE,"E247.MirrorCS"),sQuery(id+"F0.wireOp",EDGE,"E249.MirrorCS")])],"isStart":false});
            var Q1;
            Q1=makeQuery(id+"F1.opExtrude","SWEPT_EDGE",EDGE,{"disambiguationData":[OSD([sQuery(id+"F0.wireOp",EDGE,"E0.top"),sQuery(id+"F0.wireOp",EDGE,"E0.left")])]});
            var Q2;
            Q2=makeQuery(id+"F1.opExtrude","SWEPT_EDGE",EDGE,{"disambiguationData":[OSD([sQuery(id+"F0.wireOp",EDGE,"E0.top"),sQuery(id+"F0.wireOp",EDGE,"E0.right")])]});
            var Q3;
            Q3=makeQuery(id+"F1.opExtrude","SWEPT_EDGE",EDGE,{"disambiguationData":[OSD([sQuery(id+"F0.wireOp",EDGE,"E0.bottom"),sQuery(id+"F0.wireOp",EDGE,"E0.right")])]});
            var Q4;
            Q4=makeQuery(id+"F1.opExtrude","SWEPT_EDGE",EDGE,{"disambiguationData":[OSD([sQuery(id+"F0.wireOp",EDGE,"E0.bottom"),sQuery(id+"F0.wireOp",EDGE,"E0.left")])]});
            fillet(context, id + "F2", {"entities" : qUnion([Q0, Q1, Q2, Q3, Q4]), "radius" : 1.27 * mm, "tangentPropagation" : true, "allowEdgeOverflow" : false});
        }
    });
